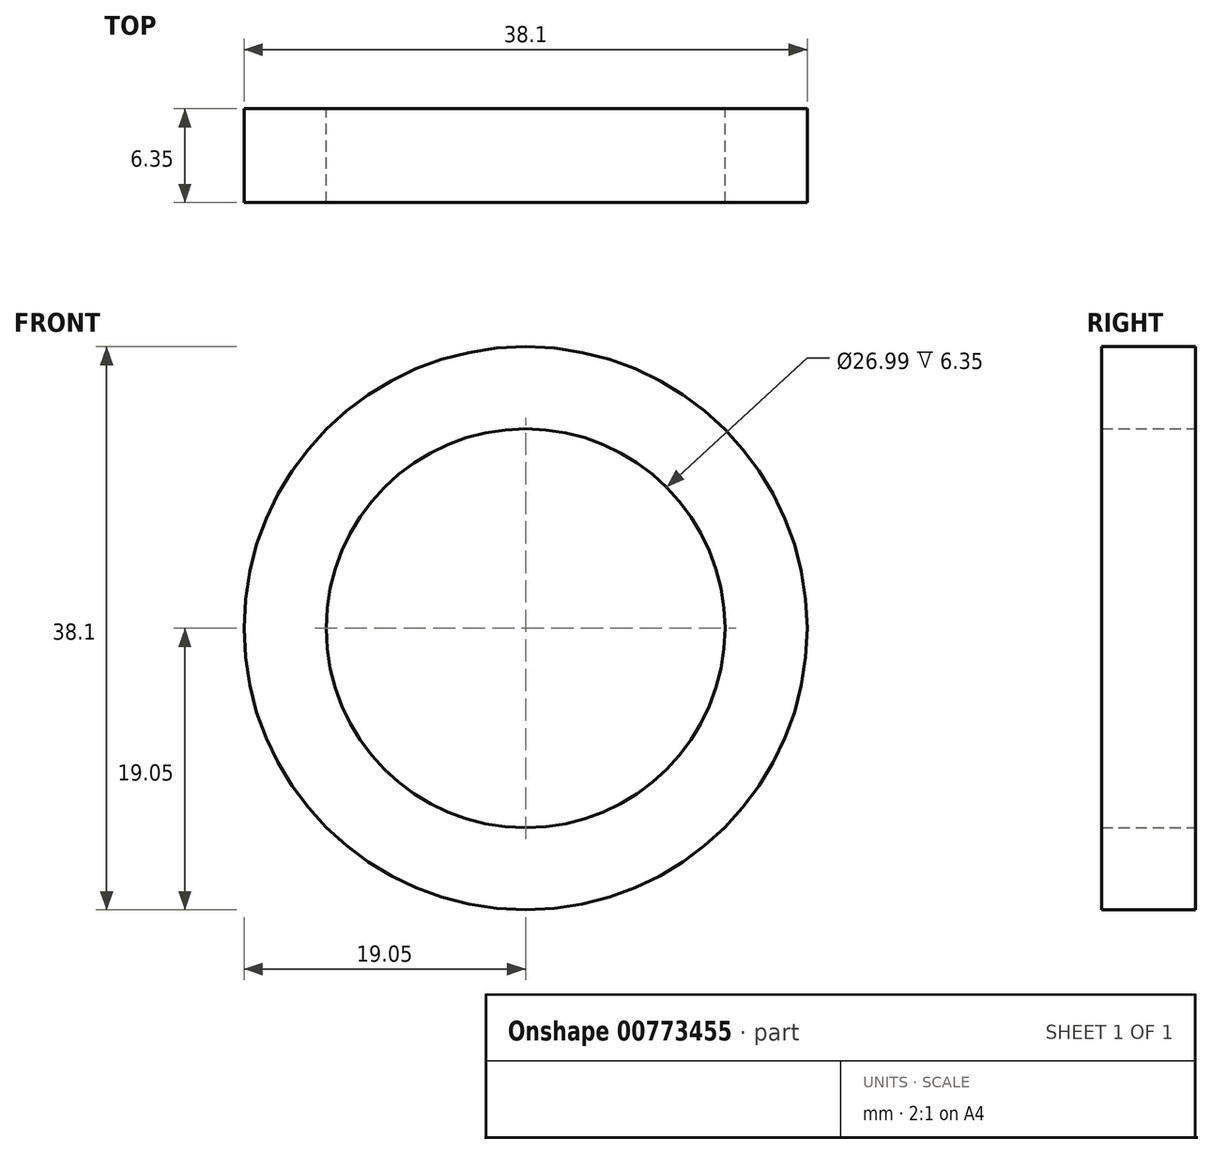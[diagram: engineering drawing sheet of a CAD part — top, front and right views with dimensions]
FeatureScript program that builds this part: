
annotation { "Feature Type Name" : "Feature", "Feature Type Description" : "" }
export const myFeature = defineFeature(function(context is Context, id is Id, definition is map)
    precondition{}
    {
        {
            var Q0;
            Q0=qCreatedBy(makeId("Front.planeOp"),FACE);
            var sketch = newSketch(context, id + "F0", { "sketchPlane" : qUnion([Q0])});
            skCircle(sketch, "E0", {"center": v(0, 0) * mm, "radius": 13.5 * mm});
            skCircle(sketch, "E1", {"center": v(0, 0) * mm, "radius": 19.05 * mm});
            skSolve(sketch);
        }
        {
            var Q0;
            Q0 = qSketchRegion(id + "F0", true);
            extrude(context, id + "F1", {"entities" : qUnion([Q0]), "depth" : 6.35 * mm, "offsetDistance" : 25.4 * mm});
        }
    });
